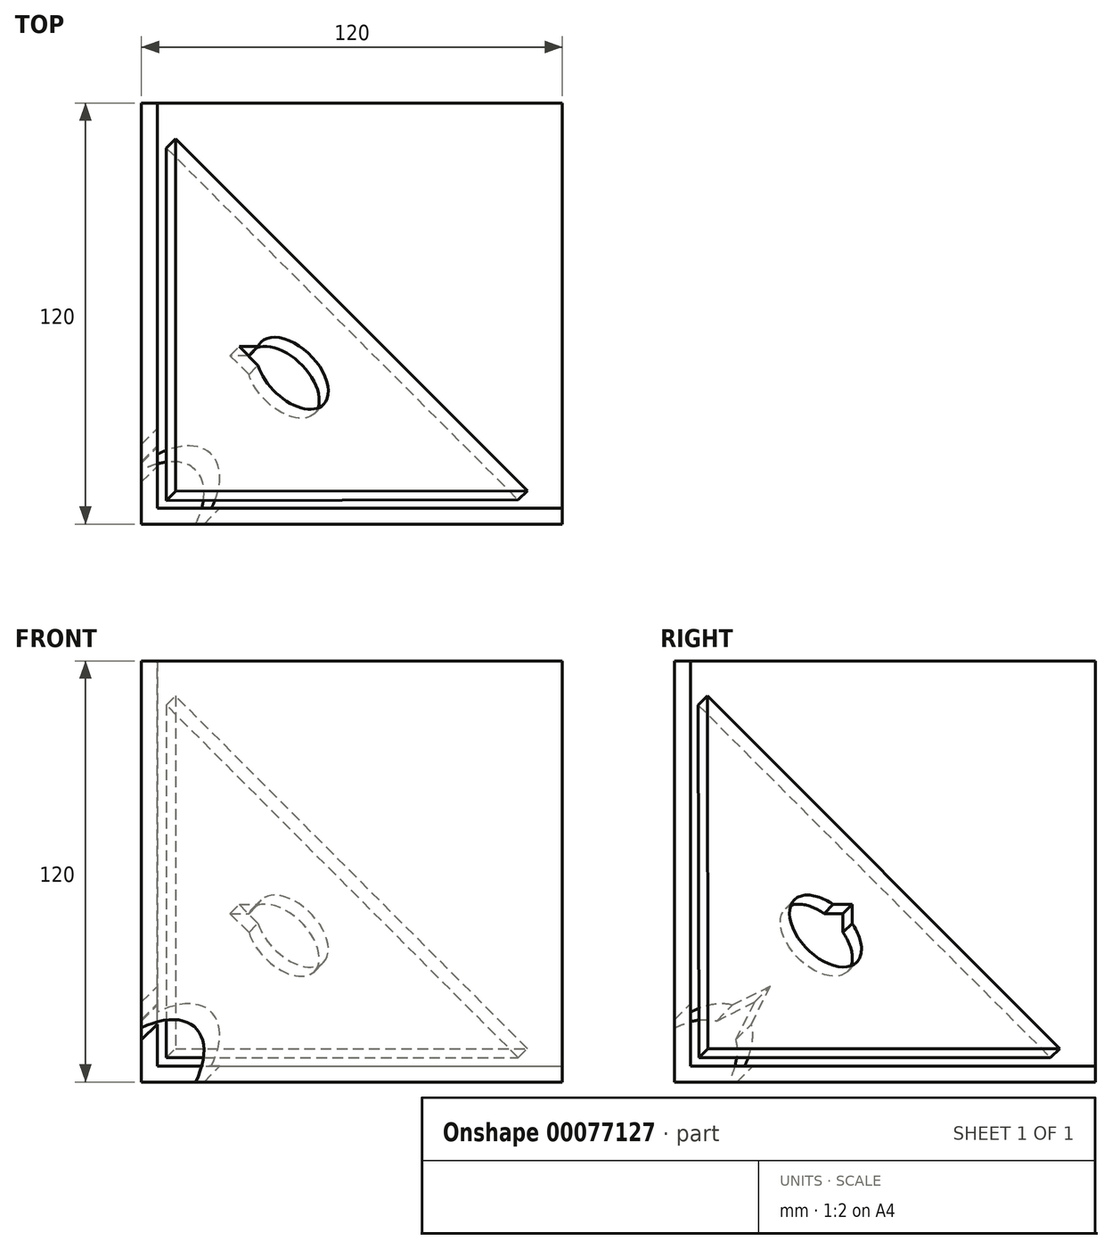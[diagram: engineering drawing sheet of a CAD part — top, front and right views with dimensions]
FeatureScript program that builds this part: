
annotation { "Feature Type Name" : "Feature", "Feature Type Description" : "" }
export const myFeature = defineFeature(function(context is Context, id is Id, definition is map)
    precondition{}
    {
        {
            var Q0;
            Q0=qCreatedBy(makeId("Front.planeOp"),FACE);
            var sketch = newSketch(context, id + "F0", { "sketchPlane" : qUnion([Q0])});
            skLineSegment(sketch, "E0.bottom", {"start": v(0, 0) * mm, "end": v(120, 0) * mm});
            skLineSegment(sketch, "E0.top", {"start": v(0, 120) * mm, "end": v(120, 120) * mm});
            skLineSegment(sketch, "E0.left", {"start": v(0, 0) * mm, "end": v(0, 120) * mm});
            skLineSegment(sketch, "E0.right", {"start": v(120, 0) * mm, "end": v(120, 120) * mm});
            skSolve(sketch);
        }
        {
            var Q0;
            Q0=qCreatedBy(makeId("Right.planeOp"),FACE);
            var sketch = newSketch(context, id + "F1", { "sketchPlane" : qUnion([Q0])});
            skLineSegment(sketch, "E1.bottom", {"start": v(0, 0) * mm, "end": v(120, 0) * mm});
            skLineSegment(sketch, "E1.top", {"start": v(0, 120) * mm, "end": v(120, 120) * mm});
            skLineSegment(sketch, "E1.left", {"start": v(0, 0) * mm, "end": v(0, 120) * mm});
            skLineSegment(sketch, "E1.right", {"start": v(120, 0) * mm, "end": v(120, 120) * mm});
            skSolve(sketch);
        }
        {
            var Q0;
            Q0=qCreatedBy(makeId("Top.planeOp"),FACE);
            var sketch = newSketch(context, id + "F2", { "sketchPlane" : qUnion([Q0])});
            skLineSegment(sketch, "E2.bottom", {"start": v(0, 0) * mm, "end": v(120, 0) * mm});
            skLineSegment(sketch, "E2.top", {"start": v(0, 120) * mm, "end": v(120, 120) * mm});
            skLineSegment(sketch, "E2.left", {"start": v(0, 0) * mm, "end": v(0, 120) * mm});
            skLineSegment(sketch, "E2.right", {"start": v(120, 0) * mm, "end": v(120, 120) * mm});
            skSolve(sketch);
        }
        {
            var Q0;
            Q0=makeQuery(id+"F2.imprint","IMPRINT",FACE,{"disambiguationData":[TD([[makeQuery(id+"F2.imprint","IMPRINT",EDGE,{"derivedFrom":sQuery(id+"F2.wireOp",EDGE,"E2.bottom")}),1.0]])]});
            extrude(context, id + "F3", {"entities" : qUnion([Q0]), "depth" : 4.5 * mm, "offsetDistance" : 25 * mm});
        }
        {
            var Q0;
            Q0=makeQuery(id+"F1.imprint","IMPRINT",FACE,{"disambiguationData":[TD([[makeQuery(id+"F1.imprint","IMPRINT",EDGE,{"derivedFrom":sQuery(id+"F1.wireOp",EDGE,"E1.bottom")}),1.0]])]});
            extrude(context, id + "F4", {"entities" : qUnion([Q0]), "operationType" : NewBodyOperationType.ADD, "depth" : 4.5 * mm, "offsetDistance" : 25 * mm});
        }
        {
            var Q0;
            Q0=makeQuery(id+"F0.imprint","IMPRINT",FACE,{"disambiguationData":[TD([[makeQuery(id+"F0.imprint","IMPRINT",EDGE,{"derivedFrom":sQuery(id+"F0.wireOp",EDGE,"E0.bottom")}),1.0]])]});
            extrude(context, id + "F5", {"entities" : qUnion([Q0]), "operationType" : NewBodyOperationType.ADD, "oppositeDirection" : true, "depth" : 4.5 * mm, "offsetDistance" : 25 * mm});
        }
        {
            var Q0;
            Q0=makeQuery(id+"F5.boolean.opBoolean","INTERSECT",VERTEX,{"derivedFrom":[makeQuery(id+"F3.opExtrude","CAP_FACE",FACE,{"disambiguationData":[OSD([sQuery(id+"F2.wireOp",EDGE,"E2.bottom"),sQuery(id+"F2.wireOp",EDGE,"E2.top"),sQuery(id+"F2.wireOp",EDGE,"E2.left"),sQuery(id+"F2.wireOp",EDGE,"E2.right")])],"isStart":false}),makeQuery(id+"F5.opExtrude","CAP_FACE",FACE,{"disambiguationData":[OSD([sQuery(id+"F0.wireOp",EDGE,"E0.bottom"),sQuery(id+"F0.wireOp",EDGE,"E0.top"),sQuery(id+"F0.wireOp",EDGE,"E0.left"),sQuery(id+"F0.wireOp",EDGE,"E0.right")])],"isStart":false})]});
            var Q1;
            Q1=makeQuery(id+"F4.boolean.opBoolean","INTERSECT",VERTEX,{"disambiguationData":[OD(1.0)],"derivedFrom":[makeQuery(id+"F3.opExtrude","CAP_FACE",FACE,{"disambiguationData":[OSD([sQuery(id+"F2.wireOp",EDGE,"E2.bottom"),sQuery(id+"F2.wireOp",EDGE,"E2.top"),sQuery(id+"F2.wireOp",EDGE,"E2.left"),sQuery(id+"F2.wireOp",EDGE,"E2.right")])],"isStart":false}),makeQuery(id+"F4.opExtrude","CAP_FACE",FACE,{"disambiguationData":[OSD([sQuery(id+"F1.wireOp",EDGE,"E1.bottom"),sQuery(id+"F1.wireOp",EDGE,"E1.top"),sQuery(id+"F1.wireOp",EDGE,"E1.left"),sQuery(id+"F1.wireOp",EDGE,"E1.right")])],"isStart":false})]});
            var Q2;
            Q2=makeQuery(id+"F5.boolean.opBoolean","INTERSECT",VERTEX,{"derivedFrom":[makeQuery(id+"F4.opExtrude","CAP_FACE",FACE,{"disambiguationData":[OSD([sQuery(id+"F1.wireOp",EDGE,"E1.bottom"),sQuery(id+"F1.wireOp",EDGE,"E1.top"),sQuery(id+"F1.wireOp",EDGE,"E1.left"),sQuery(id+"F1.wireOp",EDGE,"E1.right")])],"isStart":false}),makeQuery(id+"F5.opExtrude","CAP_FACE",FACE,{"disambiguationData":[OSD([sQuery(id+"F0.wireOp",EDGE,"E0.bottom"),sQuery(id+"F0.wireOp",EDGE,"E0.top"),sQuery(id+"F0.wireOp",EDGE,"E0.left"),sQuery(id+"F0.wireOp",EDGE,"E0.right")])],"isStart":false})]});
            cPlane(context, id + "F6", {"entities" : qUnion([Q0, Q1, Q2]), "cplaneType" : CPlaneType.THREE_POINT, "offset" : 25 * mm, "width" : 150 * mm, "height" : 150 * mm});
        }
        {
            var Q0;
            Q0=qCreatedBy(id+"F6.planeOp",FACE);
            var sketch = newSketch(context, id + "F7", { "sketchPlane" : qUnion([Q0])});
            skArc(sketch, "E3", {"start": v(-11.99, -3.8) * mm, "mid": v(12.57, 0) * mm, "end": v(-11.99, 3.8) * mm});
            skPoint(sketch, "E4.0.midPoint", {"position": v(-11.14, 0.31) * mm});
            skPoint(sketch, "E5.0.midPoint", {"position": v(-5.23, 8.61) * mm});
            skLineSegment(sketch, "E6", {"start": v(94.02, 0) * mm, "end": v(-46.81, 81.62) * mm});
            skLineSegment(sketch, "E7", {"start": v(-46.81, 81.62) * mm, "end": v(-46.81, -81.29) * mm});
            skLineSegment(sketch, "E8", {"start": v(-46.81, -81.29) * mm, "end": v(94.02, 0) * mm});
            skLineSegment(sketch, "E9.0", {"start": v(82.04, 0.01) * mm, "end": v(-40.81, 71.2) * mm});
            skLineSegment(sketch, "E9.1", {"start": v(-40.81, -70.9) * mm, "end": v(82.04, 0.01) * mm});
            skLineSegment(sketch, "E9.2", {"start": v(-40.81, 71.2) * mm, "end": v(-40.81, -70.9) * mm});
            skLineSegment(sketch, "E10.1", {"start": v(-11.99, -3.8) * mm, "end": v(-18.58, 0) * mm});
            skLineSegment(sketch, "E10.2", {"start": v(-18.58, 0) * mm, "end": v(-11.99, 3.8) * mm});
            skPoint(sketch, "E10.0.midPoint", {"position": v(-9.57, 0) * mm});
            skPoint(sketch, "E11.orphan", {"position": v(-9.57, -5.2) * mm});
            skPoint(sketch, "E12.orphan", {"position": v(-9.58, 5.2) * mm});
            skPoint(sketch, "E10.cCircle.center.orphan", {"position": v(-12.57, 0) * mm});
            skSolve(sketch);
        }
        {
            var Q0;
            Q0=makeQuery(id+"F7.imprint","IMPRINT",FACE,{"disambiguationData":[TD([[makeQuery(id+"F7.imprint","IMPRINT",EDGE,{"derivedFrom":sQuery(id+"F7.wireOp",EDGE,"E3")}),-1.0]])]});
            extrude(context, id + "F8", {"entities" : qUnion([Q0]), "depth" : 4.5 * mm, "offsetDistance" : 25 * mm});
        }
        {
            var Q0;
            Q0=makeQuery(id+"F7.imprint","IMPRINT",FACE,{"disambiguationData":[TD([[makeQuery(id+"F7.imprint","IMPRINT",EDGE,{"derivedFrom":sQuery(id+"F7.wireOp",EDGE,"E3")}),1.0]])]});
            extrude(context, id + "F9", {"entities" : qUnion([Q0]), "operationType" : NewBodyOperationType.REMOVE, "depth" : 90 * mm, "offsetDistance" : 25 * mm});
        }
    });
